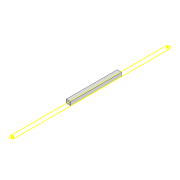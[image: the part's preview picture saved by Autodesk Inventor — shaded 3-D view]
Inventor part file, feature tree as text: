
AUTODESK INVENTOR PART (.ipt)
format: ipt  version: 2022 (Build 260153000, 153)  size: 103,424 bytes
history: native  units: mm
features: sketch x3, extrude x2, projected_geometry x1
ambient origin geometry x8: Origin, YZ Plane, XZ Plane, XY Plane, X Axis, Y Axis, Z Axis, Center Point
bodies: Solid1 (feature_tree)
feature tree (6):
  extrude  "Extrusion1"  Depth=10.0mm
  sketch  "Sketch2"  dims[d2=3.0mm d3=3.0mm]
  extrude  "Extrusion2"  Depth=3.0mm
  sketch  "Sketch1"  dims[d0=351.981mm d1=10.0mm]
  projected_geometry  "Projected Loop1"
  sketch  "Sketch3"  dims[d4=8.0mm d5=0.0mm d12=10.0mm d13=0.0mm]
